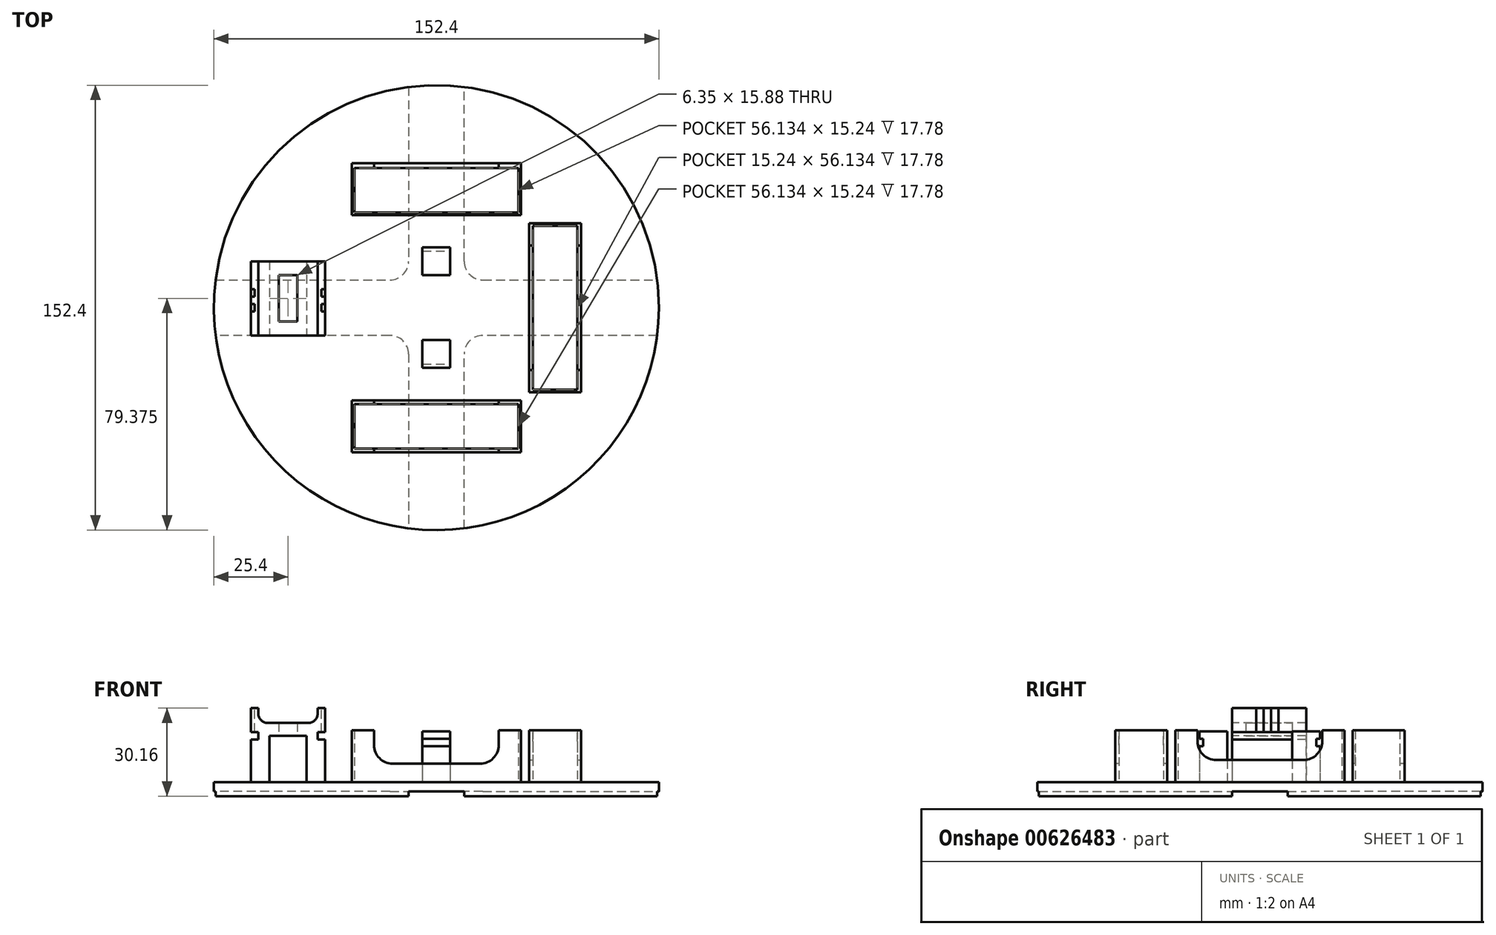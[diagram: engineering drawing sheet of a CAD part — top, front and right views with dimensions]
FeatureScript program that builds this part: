
annotation { "Feature Type Name" : "Feature", "Feature Type Description" : "" }
export const myFeature = defineFeature(function(context is Context, id is Id, definition is map)
    precondition{}
    {
        {
            var Q0;
            Q0=qCreatedBy(makeId("Top.planeOp"),FACE);
            var sketch = newSketch(context, id + "F0", { "sketchPlane" : qUnion([Q0])});
            skCircle(sketch, "E0", {"center": v(0, 0) * mm, "radius": 76.2 * mm});
            skSolve(sketch);
        }
        {
            var Q0;
            Q0 = qSketchRegion(id + "F0", true);
            extrude(context, id + "F1", {"entities" : qUnion([Q0]), "depth" : 3.17 * mm, "offsetDistance" : 25.4 * mm});
        }
        {
            var Q0;
            Q0=makeQuery(id+"F1.opExtrude","CAP_FACE",FACE,{"disambiguationData":[OSD([sQuery(id+"F0.wireOp",EDGE,"E0")])],"isStart":true});
            var sketch = newSketch(context, id + "F2", { "sketchPlane" : qUnion([Q0])});
            skLineSegment(sketch, "E1", {"start": v(-9.52, -75.6) * mm, "end": v(-9.52, -15.88) * mm});
            skLineSegment(sketch, "E2", {"start": v(9.53, 75.6) * mm, "end": v(9.53, 15.88) * mm});
            skLineSegment(sketch, "E3", {"start": v(75.6, 9.53) * mm, "end": v(15.87, 9.53) * mm});
            skLineSegment(sketch, "E4", {"start": v(-75.6, -9.53) * mm, "end": v(-15.88, -9.53) * mm});
            skLineSegment(sketch, "E5.trimOffspring", {"start": v(-15.88, 9.52) * mm, "end": v(-75.6, 9.52) * mm});
            skLineSegment(sketch, "E6.trimOffspring", {"start": v(9.53, -15.88) * mm, "end": v(9.53, -75.6) * mm});
            skLineSegment(sketch, "E7.trimOffspring", {"start": v(-9.52, 15.87) * mm, "end": v(-9.52, 75.6) * mm});
            skLineSegment(sketch, "E8.trimOffspring", {"start": v(15.87, -9.53) * mm, "end": v(75.6, -9.53) * mm});
            skPoint(sketch, "E9.visualSharp", {"position": v(9.52, 9.53) * mm});
            skArc(sketch, "E9.filletArc", {"start": v(9.52, 15.88) * mm, "mid": v(11.38, 11.38) * mm, "end": v(15.87, 9.53) * mm});
            skPoint(sketch, "E10.visualSharp", {"position": v(-9.53, 9.52) * mm});
            skArc(sketch, "E10.filletArc", {"start": v(-15.88, 9.53) * mm, "mid": v(-11.38, 11.38) * mm, "end": v(-9.53, 15.87) * mm});
            skPoint(sketch, "E11.visualSharp", {"position": v(-9.53, -9.53) * mm});
            skArc(sketch, "E11.filletArc", {"start": v(-9.53, -15.88) * mm, "mid": v(-11.38, -11.38) * mm, "end": v(-15.88, -9.53) * mm});
            skPoint(sketch, "E12.visualSharp", {"position": v(9.52, -9.53) * mm});
            skArc(sketch, "E12.filletArc", {"start": v(15.87, -9.53) * mm, "mid": v(11.38, -11.38) * mm, "end": v(9.52, -15.88) * mm});
            skArc(sketch, "E13", {"start": v(-9.52, 75.6) * mm, "mid": v(-53.88, 53.88) * mm, "end": v(-75.6, 9.52) * mm});
            skArc(sketch, "E14.trimOffspring", {"start": v(75.6, 9.52) * mm, "mid": v(53.88, 53.88) * mm, "end": v(9.53, 75.6) * mm});
            skArc(sketch, "E15.trimOffspring", {"start": v(9.53, -75.6) * mm, "mid": v(53.88, -53.88) * mm, "end": v(75.6, -9.53) * mm});
            skArc(sketch, "E16.trimOffspring", {"start": v(-75.6, -9.53) * mm, "mid": v(-53.88, -53.88) * mm, "end": v(-9.52, -75.6) * mm});
            skSolve(sketch);
        }
        {
            var Q0;
            Q0 = qSketchRegion(id + "F2", true);
            extrude(context, id + "F3", {"entities" : qUnion([Q0]), "operationType" : NewBodyOperationType.ADD, "depth" : 1.59 * mm, "offsetDistance" : 25.4 * mm});
        }
        {
            var Q0;
            Q0=makeQuery(id+"F1.opExtrude","CAP_FACE",FACE,{"disambiguationData":[OSD([sQuery(id+"F0.wireOp",EDGE,"E0")])],"isStart":false});
            var sketch = newSketch(context, id + "F4", { "sketchPlane" : qUnion([Q0])});
            skLineSegment(sketch, "E17.bottom", {"start": v(-28.96, 49.53) * mm, "end": v(28.96, 49.53) * mm});
            skLineSegment(sketch, "E17.top", {"start": v(-28.96, 31.75) * mm, "end": v(28.96, 31.75) * mm});
            skLineSegment(sketch, "E17.left", {"start": v(-28.96, 49.53) * mm, "end": v(-28.96, 31.75) * mm});
            skLineSegment(sketch, "E17.right", {"start": v(28.96, 49.53) * mm, "end": v(28.96, 31.75) * mm});
            skLineSegment(sketch, "E18.bottom", {"start": v(31.75, 28.96) * mm, "end": v(49.53, 28.96) * mm});
            skLineSegment(sketch, "E18.top", {"start": v(31.75, -28.96) * mm, "end": v(49.53, -28.96) * mm});
            skLineSegment(sketch, "E18.left", {"start": v(31.75, 28.96) * mm, "end": v(31.75, -28.96) * mm});
            skLineSegment(sketch, "E18.right", {"start": v(49.53, 28.96) * mm, "end": v(49.53, -28.96) * mm});
            skLineSegment(sketch, "E19.bottom", {"start": v(28.96, -31.75) * mm, "end": v(-28.96, -31.75) * mm});
            skLineSegment(sketch, "E19.top", {"start": v(28.96, -49.53) * mm, "end": v(-28.96, -49.53) * mm});
            skLineSegment(sketch, "E19.left", {"start": v(28.96, -31.75) * mm, "end": v(28.96, -49.53) * mm});
            skLineSegment(sketch, "E19.right", {"start": v(-28.96, -31.75) * mm, "end": v(-28.96, -49.53) * mm});
            skLineSegment(sketch, "E20.bottom", {"start": v(-28.07, 47.88) * mm, "end": v(28.07, 47.88) * mm});
            skLineSegment(sketch, "E20.top", {"start": v(-28.07, 32.64) * mm, "end": v(28.07, 32.64) * mm});
            skLineSegment(sketch, "E20.left", {"start": v(-28.07, 47.88) * mm, "end": v(-28.07, 32.64) * mm});
            skLineSegment(sketch, "E20.right", {"start": v(28.07, 47.88) * mm, "end": v(28.07, 32.64) * mm});
            skLineSegment(sketch, "E21.bottom", {"start": v(33.02, 28.07) * mm, "end": v(48.26, 28.07) * mm});
            skLineSegment(sketch, "E21.top", {"start": v(33.02, -28.07) * mm, "end": v(48.26, -28.07) * mm});
            skLineSegment(sketch, "E21.left", {"start": v(33.02, 28.07) * mm, "end": v(33.02, -28.07) * mm});
            skLineSegment(sketch, "E21.right", {"start": v(48.26, 28.07) * mm, "end": v(48.26, -28.07) * mm});
            skLineSegment(sketch, "E22.bottom", {"start": v(28.07, -33.02) * mm, "end": v(-28.07, -33.02) * mm});
            skLineSegment(sketch, "E22.top", {"start": v(28.07, -48.26) * mm, "end": v(-28.07, -48.26) * mm});
            skLineSegment(sketch, "E22.left", {"start": v(28.07, -33.02) * mm, "end": v(28.07, -48.26) * mm});
            skLineSegment(sketch, "E22.right", {"start": v(-28.07, -33.02) * mm, "end": v(-28.07, -48.26) * mm});
            skSolve(sketch);
        }
        {
            var Q0;
            Q0 = qSketchRegion(id + "F4", true);
            extrude(context, id + "F5", {"entities" : qUnion([Q0]), "operationType" : NewBodyOperationType.ADD, "depth" : 17.78 * mm, "offsetDistance" : 25.4 * mm});
        }
        {
            var Q0;
            Q0=makeQuery(id+"F5.opExtrude","SWEPT_FACE",FACE,{"disambiguationData":[OSD([sQuery(id+"F4.wireOp",EDGE,"E18.right")])]});
            var sketch = newSketch(context, id + "F6", { "sketchPlane" : qUnion([Q0])});
            skLineSegment(sketch, "E23.bottom", {"start": v(14.99, 10.8) * mm, "end": v(-14.99, 10.8) * mm});
            skLineSegment(sketch, "E23.top", {"start": v(21.34, 23.5) * mm, "end": v(-21.34, 23.5) * mm});
            skLineSegment(sketch, "E23.left", {"start": v(21.34, 17.15) * mm, "end": v(21.34, 23.5) * mm});
            skLineSegment(sketch, "E23.right", {"start": v(-21.34, 17.14) * mm, "end": v(-21.34, 23.5) * mm});
            skPoint(sketch, "E24.visualSharp", {"position": v(21.34, 10.8) * mm});
            skArc(sketch, "E24.filletArc", {"start": v(14.99, 10.8) * mm, "mid": v(19.48, 12.65) * mm, "end": v(21.34, 17.15) * mm});
            skPoint(sketch, "E25.visualSharp", {"position": v(-21.34, 10.8) * mm});
            skArc(sketch, "E25.filletArc", {"start": v(-21.34, 17.14) * mm, "mid": v(-19.48, 12.65) * mm, "end": v(-14.99, 10.8) * mm});
            skSolve(sketch);
        }
        {
            var Q0;
            Q0 = qSketchRegion(id + "F6", true);
            extrude(context, id + "F7", {"entities" : qUnion([Q0]), "operationType" : NewBodyOperationType.REMOVE, "endBound" : BoundingType.THROUGH_ALL, "oppositeDirection" : true, "depth" : 25.4 * mm, "offsetDistance" : 25.4 * mm});
        }
        {
            var Q0;
            Q0=makeQuery(id+"F5.opExtrude","SWEPT_FACE",FACE,{"disambiguationData":[OSD([sQuery(id+"F4.wireOp",EDGE,"E19.top")])]});
            var sketch = newSketch(context, id + "F8", { "sketchPlane" : qUnion([Q0])});
            skLineSegment(sketch, "E26.bottom", {"start": v(-14.99, 9.53) * mm, "end": v(14.99, 9.53) * mm});
            skLineSegment(sketch, "E26.top", {"start": v(-21.34, 22.23) * mm, "end": v(21.34, 22.23) * mm});
            skLineSegment(sketch, "E26.left", {"start": v(-21.34, 15.88) * mm, "end": v(-21.34, 22.23) * mm});
            skLineSegment(sketch, "E26.right", {"start": v(21.34, 15.88) * mm, "end": v(21.34, 22.23) * mm});
            skPoint(sketch, "E27.visualSharp", {"position": v(-21.34, 9.53) * mm});
            skArc(sketch, "E27.filletArc", {"start": v(-21.34, 15.88) * mm, "mid": v(-19.48, 11.38) * mm, "end": v(-14.99, 9.52) * mm});
            skPoint(sketch, "E28.visualSharp", {"position": v(21.34, 9.53) * mm});
            skArc(sketch, "E28.filletArc", {"start": v(14.99, 9.53) * mm, "mid": v(19.48, 11.38) * mm, "end": v(21.34, 15.88) * mm});
            skSolve(sketch);
        }
        {
            var Q0;
            Q0 = qSketchRegion(id + "F8", true);
            extrude(context, id + "F9", {"entities" : qUnion([Q0]), "operationType" : NewBodyOperationType.REMOVE, "endBound" : BoundingType.THROUGH_ALL, "oppositeDirection" : true, "depth" : 25.4 * mm, "offsetDistance" : 25.4 * mm});
        }
        {
            var Q0;
            {var subQ0=sQuery(id+"F0.wireOp",EDGE,"E0");Q0=makeQuery(id+"F5.boolean.opBoolean","SPLIT",FACE,{"disambiguationData":[TD([makeQuery(id+"F1.opExtrude","SWEPT_FACE",FACE,{"disambiguationData":[OSD([subQ0])]})])],"derivedFrom":makeQuery(id+"F1.opExtrude","CAP_FACE",FACE,{"disambiguationData":[OSD([subQ0])],"isStart":false})});}
            var sketch = newSketch(context, id + "F10", { "sketchPlane" : qUnion([Q0])});
            skLineSegment(sketch, "E29.bottom", {"start": v(-63.5, 15.88) * mm, "end": v(-38.1, 15.88) * mm});
            skLineSegment(sketch, "E29.top", {"start": v(-63.5, -9.53) * mm, "end": v(-38.1, -9.53) * mm});
            skLineSegment(sketch, "E29.left", {"start": v(-63.5, 15.88) * mm, "end": v(-63.5, -9.53) * mm});
            skLineSegment(sketch, "E29.right", {"start": v(-38.1, 15.88) * mm, "end": v(-38.1, -9.53) * mm});
            skLineSegment(sketch, "E30.bottom", {"start": v(-53.98, 11.11) * mm, "end": v(-47.63, 11.11) * mm});
            skLineSegment(sketch, "E30.top", {"start": v(-53.98, -4.76) * mm, "end": v(-47.63, -4.76) * mm});
            skLineSegment(sketch, "E30.left", {"start": v(-53.98, 11.11) * mm, "end": v(-53.98, -4.76) * mm});
            skLineSegment(sketch, "E30.right", {"start": v(-47.63, 11.11) * mm, "end": v(-47.63, -4.76) * mm});
            skSolve(sketch);
        }
        {
            var Q0;
            Q0 = qSketchRegion(id + "F10", true);
            extrude(context, id + "F11", {"entities" : qUnion([Q0]), "operationType" : NewBodyOperationType.ADD, "depth" : 25.4 * mm, "offsetDistance" : 25.4 * mm});
        }
        {
            var Q0;
            Q0=makeQuery(id+"F11.opExtrude","SWEPT_FACE",FACE,{"disambiguationData":[OSD([sQuery(id+"F10.wireOp",EDGE,"E29.top")])]});
            var sketch = newSketch(context, id + "F12", { "sketchPlane" : qUnion([Q0])});
            skLineSegment(sketch, "E31.bottom", {"start": v(-60.96, 48.9) * mm, "end": v(-40.64, 48.9) * mm});
            skLineSegment(sketch, "E31.top", {"start": v(-57.79, 23.5) * mm, "end": v(-43.81, 23.5) * mm});
            skLineSegment(sketch, "E31.left", {"start": v(-60.96, 48.9) * mm, "end": v(-60.96, 26.67) * mm});
            skLineSegment(sketch, "E31.right", {"start": v(-40.64, 48.9) * mm, "end": v(-40.64, 26.67) * mm});
            skPoint(sketch, "E32.visualSharp", {"position": v(-60.96, 23.5) * mm});
            skArc(sketch, "E32.filletArc", {"start": v(-60.96, 26.67) * mm, "mid": v(-60.03, 24.42) * mm, "end": v(-57.79, 23.5) * mm});
            skPoint(sketch, "E33.visualSharp", {"position": v(-40.64, 23.5) * mm});
            skArc(sketch, "E33.filletArc", {"start": v(-43.81, 23.5) * mm, "mid": v(-41.57, 24.42) * mm, "end": v(-40.64, 26.67) * mm});
            skLineSegment(sketch, "E34.bottom", {"start": v(-57.15, 3.18) * mm, "end": v(-44.45, 3.18) * mm});
            skLineSegment(sketch, "E34.top", {"start": v(-57.15, 19.05) * mm, "end": v(-44.45, 19.05) * mm});
            skLineSegment(sketch, "E34.left", {"start": v(-57.15, 3.18) * mm, "end": v(-57.15, 19.05) * mm});
            skLineSegment(sketch, "E34.right", {"start": v(-44.45, 3.18) * mm, "end": v(-44.45, 19.05) * mm});
            skLineSegment(sketch, "E35.bottom", {"start": v(-63.5, 20.32) * mm, "end": v(-60.96, 20.32) * mm});
            skLineSegment(sketch, "E35.top", {"start": v(-63.5, 17.78) * mm, "end": v(-60.96, 17.78) * mm});
            skLineSegment(sketch, "E35.left", {"start": v(-63.5, 20.32) * mm, "end": v(-63.5, 17.78) * mm});
            skLineSegment(sketch, "E35.right", {"start": v(-60.96, 20.32) * mm, "end": v(-60.96, 17.78) * mm});
            skLineSegment(sketch, "E36.bottom", {"start": v(-38.1, 20.32) * mm, "end": v(-40.64, 20.32) * mm});
            skLineSegment(sketch, "E36.top", {"start": v(-38.1, 17.78) * mm, "end": v(-40.64, 17.78) * mm});
            skLineSegment(sketch, "E36.left", {"start": v(-38.1, 20.32) * mm, "end": v(-38.1, 17.78) * mm});
            skLineSegment(sketch, "E36.right", {"start": v(-40.64, 20.32) * mm, "end": v(-40.64, 17.78) * mm});
            skSolve(sketch);
        }
        {
            var Q0;
            Q0=makeQuery(id+"F12.imprint","IMPRINT",FACE,{"disambiguationData":[TD([[makeQuery(id+"F12.imprint","IMPRINT",EDGE,{"derivedFrom":sQuery(id+"F12.wireOp",EDGE,"E31.top")}),1.0]])]});
            var Q1;
            Q1=makeQuery(id+"F12.imprint","IMPRINT",FACE,{"disambiguationData":[TD([[makeQuery(id+"F12.imprint","IMPRINT",EDGE,{"derivedFrom":sQuery(id+"F12.wireOp",EDGE,"E34.bottom")}),1.0]])]});
            var Q2;
            Q2=makeQuery(id+"F12.imprint","IMPRINT",FACE,{"disambiguationData":[TD([[makeQuery(id+"F12.imprint","IMPRINT",EDGE,{"derivedFrom":sQuery(id+"F12.wireOp",EDGE,"E35.bottom")}),-1.0]])]});
            var Q3;
            Q3=makeQuery(id+"F12.imprint","IMPRINT",FACE,{"disambiguationData":[TD([[makeQuery(id+"F12.imprint","IMPRINT",EDGE,{"derivedFrom":sQuery(id+"F12.wireOp",EDGE,"E36.bottom")}),1.0]])]});
            var Q4;
            Q4=makeQuery(id+"F11.opExtrude","SWEPT_FACE",FACE,{"disambiguationData":[OSD([sQuery(id+"F10.wireOp",EDGE,"E29.bottom")])]});
            extrude(context, id + "F13", {"entities" : qUnion([Q0, Q1, Q2, Q3]), "operationType" : NewBodyOperationType.REMOVE, "endBound" : BoundingType.UP_TO_SURFACE, "oppositeDirection" : true, "depth" : 25.4 * mm, "endBoundEntityFace" : qUnion([Q4]), "offsetDistance" : 25.4 * mm});
        }
        {
            var Q0;
            {var subQ0=sQuery(id+"F0.wireOp",EDGE,"E0");Q0=makeQuery(id+"F5.boolean.opBoolean","SPLIT",FACE,{"disambiguationData":[TD([makeQuery(id+"F1.opExtrude","SWEPT_FACE",FACE,{"disambiguationData":[OSD([subQ0])]})])],"derivedFrom":makeQuery(id+"F1.opExtrude","CAP_FACE",FACE,{"disambiguationData":[OSD([subQ0])],"isStart":false})});}
            var sketch = newSketch(context, id + "F14", { "sketchPlane" : qUnion([Q0])});
            skLineSegment(sketch, "E37.bottom", {"start": v(-4.76, -11.11) * mm, "end": v(4.76, -11.11) * mm});
            skLineSegment(sketch, "E37.top", {"start": v(-4.76, -20.64) * mm, "end": v(4.76, -20.64) * mm});
            skLineSegment(sketch, "E37.left", {"start": v(-4.76, -11.11) * mm, "end": v(-4.76, -20.64) * mm});
            skLineSegment(sketch, "E37.right", {"start": v(4.76, -11.11) * mm, "end": v(4.76, -20.64) * mm});
            skLineSegment(sketch, "E38.bottom", {"start": v(-4.76, 20.64) * mm, "end": v(4.76, 20.64) * mm});
            skLineSegment(sketch, "E38.top", {"start": v(-4.76, 11.11) * mm, "end": v(4.76, 11.11) * mm});
            skLineSegment(sketch, "E38.left", {"start": v(-4.76, 20.64) * mm, "end": v(-4.76, 11.11) * mm});
            skLineSegment(sketch, "E38.right", {"start": v(4.76, 20.64) * mm, "end": v(4.76, 11.11) * mm});
            skLineSegment(sketch, "E39", {"start": v(0, 0) * mm, "end": v(0, -3.95) * mm, "construction": true});
            skLineSegment(sketch, "E40", {"start": v(0, 0) * mm, "end": v(3.55, 0) * mm, "construction": true});
            skSolve(sketch);
        }
        {
            var Q0;
            Q0 = qSketchRegion(id + "F14", true);
            extrude(context, id + "F15", {"entities" : qUnion([Q0]), "operationType" : NewBodyOperationType.ADD, "depth" : 17.46 * mm, "offsetDistance" : 25.4 * mm});
        }
        {
            var Q0;
            Q0=makeQuery(id+"F15.opExtrude","SWEPT_FACE",FACE,{"disambiguationData":[OSD([sQuery(id+"F14.wireOp",EDGE,"E38.right")])]});
            var sketch = newSketch(context, id + "F16", { "sketchPlane" : qUnion([Q0])});
            skLineSegment(sketch, "E41", {"start": v(20.64, 18.1) * mm, "end": v(19.37, 18.1) * mm});
            skLineSegment(sketch, "E42", {"start": v(19.37, 18.1) * mm, "end": v(19.37, 15.56) * mm});
            skLineSegment(sketch, "E43", {"start": v(19.37, 15.56) * mm, "end": v(20.64, 15.56) * mm});
            skLineSegment(sketch, "E44", {"start": v(20.64, 15.56) * mm, "end": v(20.64, 18.1) * mm});
            skLineSegment(sketch, "E45.bottom", {"start": v(-20.64, 18.1) * mm, "end": v(-19.37, 18.1) * mm});
            skLineSegment(sketch, "E45.top", {"start": v(-20.64, 15.56) * mm, "end": v(-19.37, 15.56) * mm});
            skLineSegment(sketch, "E45.left", {"start": v(-20.64, 18.1) * mm, "end": v(-20.64, 15.56) * mm});
            skLineSegment(sketch, "E45.right", {"start": v(-19.37, 18.1) * mm, "end": v(-19.37, 15.56) * mm});
            skSolve(sketch);
        }
        {
            var Q0;
            Q0 = qSketchRegion(id + "F16", true);
            var Q1;
            Q1=makeQuery(id+"F15.opExtrude","SWEPT_FACE",FACE,{"disambiguationData":[OSD([sQuery(id+"F14.wireOp",EDGE,"E37.left")])]});
            extrude(context, id + "F17", {"entities" : qUnion([Q0]), "operationType" : NewBodyOperationType.REMOVE, "oppositeDirection" : true, "depth" : 25.4 * mm, "endBoundEntityFace" : qUnion([Q1]), "offsetDistance" : 25.4 * mm});
        }
        {
            var Q0;
            {var subQ0=sQuery(id+"F10.wireOp",EDGE,"E29.bottom");var subQ1=sQuery(id+"F10.wireOp",EDGE,"E29.top");var subQ2=sQuery(id+"F10.wireOp",EDGE,"E29.left");Q0=makeQuery(id+"F13.boolean.opBoolean","SPLIT",FACE,{"disambiguationData":[TD([makeQuery(id+"F11.opExtrude","SWEPT_FACE",FACE,{"disambiguationData":[OSD([subQ2])]})])],"derivedFrom":makeQuery(id+"F11.opExtrude","CAP_FACE",FACE,{"disambiguationData":[OSD([subQ0,subQ1,subQ2,sQuery(id+"F10.wireOp",EDGE,"E29.right"),sQuery(id+"F10.wireOp",EDGE,"E30.bottom"),sQuery(id+"F10.wireOp",EDGE,"E30.top"),sQuery(id+"F10.wireOp",EDGE,"E30.left"),sQuery(id+"F10.wireOp",EDGE,"E30.right")])],"isStart":false})});}
            var sketch = newSketch(context, id + "F18", { "sketchPlane" : qUnion([Q0])});
            skLineSegment(sketch, "E46.bottom", {"start": v(-63.5, 6.35) * mm, "end": v(-62.23, 6.35) * mm});
            skLineSegment(sketch, "E46.top", {"start": v(-63.5, 3.8) * mm, "end": v(-62.23, 3.8) * mm});
            skLineSegment(sketch, "E46.left", {"start": v(-63.5, 6.35) * mm, "end": v(-63.5, 3.8) * mm});
            skLineSegment(sketch, "E46.right", {"start": v(-62.23, 6.35) * mm, "end": v(-62.23, 3.8) * mm});
            skLineSegment(sketch, "E47.bottom", {"start": v(-63.5, 1.27) * mm, "end": v(-62.23, 1.27) * mm});
            skLineSegment(sketch, "E47.top", {"start": v(-63.5, -1.27) * mm, "end": v(-62.23, -1.27) * mm});
            skLineSegment(sketch, "E47.left", {"start": v(-63.5, 1.27) * mm, "end": v(-63.5, -1.27) * mm});
            skLineSegment(sketch, "E47.right", {"start": v(-62.23, 1.27) * mm, "end": v(-62.23, -1.27) * mm});
            skLineSegment(sketch, "E48.bottom", {"start": v(-38.1, 6.35) * mm, "end": v(-39.37, 6.35) * mm});
            skLineSegment(sketch, "E48.top", {"start": v(-38.1, 3.8) * mm, "end": v(-39.37, 3.8) * mm});
            skLineSegment(sketch, "E48.left", {"start": v(-38.1, 6.35) * mm, "end": v(-38.1, 3.8) * mm});
            skLineSegment(sketch, "E48.right", {"start": v(-39.37, 6.35) * mm, "end": v(-39.37, 3.8) * mm});
            skLineSegment(sketch, "E49.bottom", {"start": v(-38.1, 1.27) * mm, "end": v(-39.37, 1.27) * mm});
            skLineSegment(sketch, "E49.top", {"start": v(-38.1, -1.27) * mm, "end": v(-39.37, -1.27) * mm});
            skLineSegment(sketch, "E49.left", {"start": v(-38.1, 1.27) * mm, "end": v(-38.1, -1.27) * mm});
            skLineSegment(sketch, "E49.right", {"start": v(-39.37, 1.27) * mm, "end": v(-39.37, -1.27) * mm});
            skSolve(sketch);
        }
        {
            var Q0;
            Q0 = qSketchRegion(id + "F18", true);
            var Q1;
            Q1=makeQuery(id+"F13.boolean.opBoolean","COPY",FACE,{"derivedFrom":makeQuery(id+"F13.opExtrude","SWEPT_FACE",FACE,{"disambiguationData":[OSD([sQuery(id+"F12.wireOp",EDGE,"E36.bottom")])]})});
            extrude(context, id + "F19", {"entities" : qUnion([Q0]), "operationType" : NewBodyOperationType.REMOVE, "endBound" : BoundingType.UP_TO_SURFACE, "oppositeDirection" : true, "depth" : 25.4 * mm, "endBoundEntityFace" : qUnion([Q1]), "offsetDistance" : 25.4 * mm});
        }
    });
